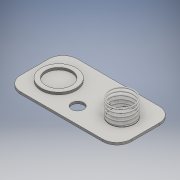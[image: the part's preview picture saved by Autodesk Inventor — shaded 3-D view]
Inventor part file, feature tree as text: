
AUTODESK INVENTOR PART (.ipt)
format: ipt  version: 2016 (Build 200138000, 138)  size: 339,456 bytes
history: native  units: mm
features: sketch x4, extrude x3, plane x1, helix x1
ambient origin geometry x8: Origin, YZ Plane, XZ Plane, XY Plane, X Axis, Y Axis, Z Axis, Center Point
bodies: Solid1 (feature_tree)
feature tree (9):
  extrude  "Extrusion1"  Depth=12.57mm
  plane  "Work Plane1"
  helix  "Coil1"  [1 undecoded]
  extrude  "Extrusion2"  Depth=3.56mm
  extrude  "Extrusion3"  Depth=0.51mm TaperAngle=0.0deg
  sketch  "Sketch1"  dims[d0=24.51mm d1=12.57mm d2=3.18mm]
  sketch  "Sketch3"  dims[d3=2.69mm d4=3.56mm]
  sketch  "Sketch4"  dims[d5=12.255mm d6=0.51mm d7=0.0mm]
  sketch  "Sketch5"  dims[d8=-5.255mm d9=0.254mm d10=6.35mm d11=2.68mm d13=0.0mm d14=0.762mm d15=10.0mm d16=50.0mm d17=0.0mm d18=90.0deg d19=90.0deg d20=0.0mm d21=0.0mm d22=6.35mm d23=5.255mm d24=1.0mm d25=5.75mm d26=0.5mm d27=0.0mm d28=6.35mm d29=5.255mm d30=0.1mm d31=0.0mm]
note: 1 required parameter value undecoded (feature->parameter linkage not recoverable at this tier; creation-order binding heuristic only, values carry confidence <= 0.55)
